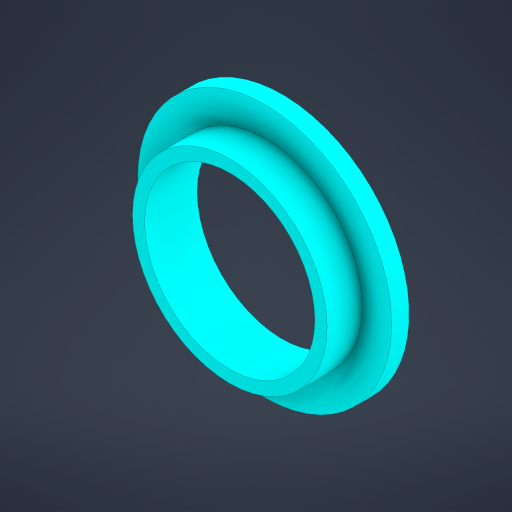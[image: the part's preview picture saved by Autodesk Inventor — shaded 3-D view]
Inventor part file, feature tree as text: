
AUTODESK INVENTOR PART (.ipt)
format: ipt  version: 2023.4 (Build 274418000, 418)  size: 212,480 bytes
history: native  units: mm
features: other x3, sketch x2, extrude x2, plane x1, reference x1
ambient origin geometry x8: Origin, YZ Plane, XZ Plane, XY Plane, X Axis, Y Axis, Z Axis, Center Point
bodies: Solid1 (feature_tree)
feature tree (9):
  sketch  "Sketch1"  dims[d0=0.035mm d2=0.875mm]
  plane  "Work Plane1"
  extrude  "Extrusion1"  Depth=0.875mm
  extrude  "Extrusion2"  Depth=1.25mm
  reference  "Reference1"
  sketch  "Sketch2"  dims[d3=2.5mm d4=0.0mm d5=0.125mm d6=2.0mm d7=1.25mm d8=0.0mm]
  other  "<path>\Projects\Project Protocube\Protocube\CAD, STL, OBJ Files\1 CAD\Cube 1x1 V5.iam"
  other  "Cube 1x1 V5.iam"
  other  "Half Inch Lense Holder (V5):1"
note: 1 file-system path scrubbed to <path> (originals preserved in map.json)
